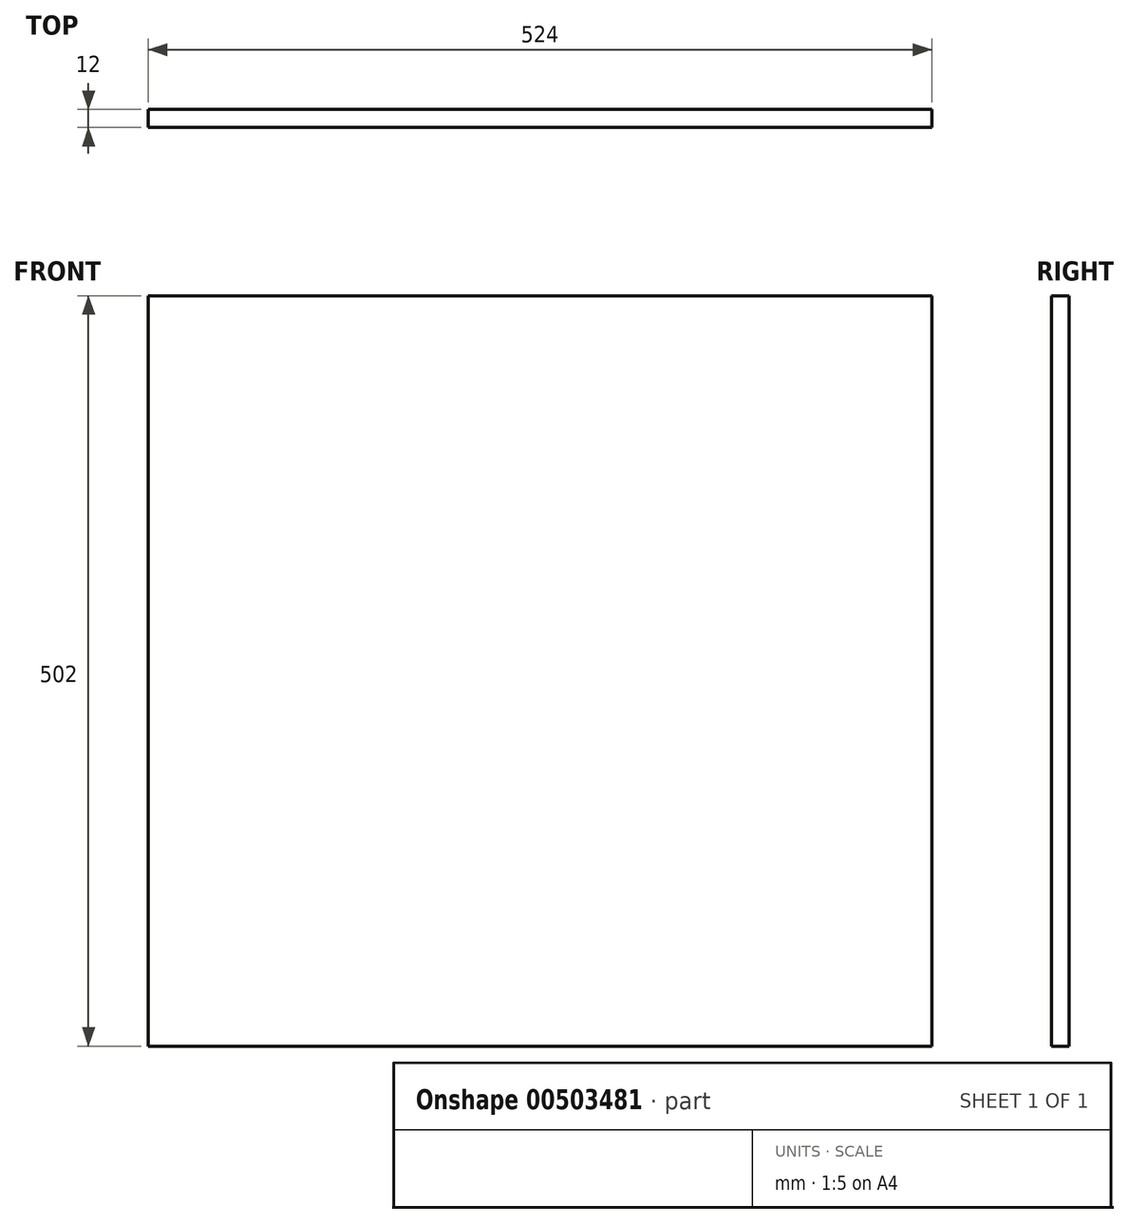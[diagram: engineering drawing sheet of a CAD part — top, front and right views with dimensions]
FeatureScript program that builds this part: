
annotation { "Feature Type Name" : "Feature", "Feature Type Description" : "" }
export const myFeature = defineFeature(function(context is Context, id is Id, definition is map)
    precondition{}
    {
        {
            var Q0;
            Q0=qCreatedBy(makeId("Top.planeOp"),FACE);
            var sketch = newSketch(context, id + "F0", { "sketchPlane" : qUnion([Q0])});
            skLineSegment(sketch, "E0.bottom", {"start": v(250, -250) * mm, "end": v(-250, -250) * mm});
            skLineSegment(sketch, "E0.top", {"start": v(250, 250) * mm, "end": v(-250, 250) * mm});
            skLineSegment(sketch, "E0.left", {"start": v(250, -250) * mm, "end": v(250, 250) * mm});
            skLineSegment(sketch, "E0.right", {"start": v(-250, -250) * mm, "end": v(-250, 250) * mm});
            skPoint(sketch, "E0.middle", {"position": v(0, 0) * mm});
            skSolve(sketch);
        }
        {
            var Q0;
            Q0=qSketchRegion(id+"F0",true);
            extrude(context, id + "F1", {"entities" : qUnion([Q0]), "depth" : 12 * mm, "offsetDistance" : 25 * mm});
        }
        {
            var Q0;
            Q0=qCreatedBy(makeId("Right.planeOp"),FACE);
            var sketch = newSketch(context, id + "F2", { "sketchPlane" : qUnion([Q0])});
            skLineSegment(sketch, "E1.bottom", {"start": v(250, -25) * mm, "end": v(-250, -25) * mm});
            skLineSegment(sketch, "E1.top", {"start": v(250, 25) * mm, "end": v(-250, 25) * mm});
            skLineSegment(sketch, "E1.left", {"start": v(250, -25) * mm, "end": v(250, 25) * mm});
            skLineSegment(sketch, "E1.right", {"start": v(-250, -25) * mm, "end": v(-250, 25) * mm});
            skPoint(sketch, "E1.middle", {"position": v(0, 0) * mm});
            skSolve(sketch);
        }
        {
            var Q0;
            Q0=qSketchRegion(id+"F2",true);
            extrude(context, id + "F3", {"entities" : qUnion([Q0]), "endBound" : BoundingType.SYMMETRIC, "depth" : 12 * mm, "offsetDistance" : 25 * mm});
        }
        {
            var Q0;
            Q0=makeQuery(id+"F3.opExtrude","SWEPT_BODY",BODY,{"disambiguationData":[OSD([sQuery(id+"F2.wireOp",EDGE,"E1.bottom"),sQuery(id+"F2.wireOp",EDGE,"E1.top"),sQuery(id+"F2.wireOp",EDGE,"E1.left"),sQuery(id+"F2.wireOp",EDGE,"E1.right")])]});
            transform(context, id + "F4", {"entities" : qUnion([Q0]), "transformType" : TransformType.TRANSLATION_3D, "dx" : 0 * mm, "dy" : 0 * mm, "dz" : -25 * mm, "makeCopy" : false});
        }
        {
            var Q0;
            Q0=qCreatedBy(makeId("Front.planeOp"),FACE);
            var sketch = newSketch(context, id + "F5", { "sketchPlane" : qUnion([Q0])});
            skLineSegment(sketch, "E2.bottom", {"start": v(250, -25) * mm, "end": v(-250, -25) * mm});
            skLineSegment(sketch, "E2.left", {"start": v(250, -25) * mm, "end": v(250, 25) * mm});
            skLineSegment(sketch, "E2.right", {"start": v(-250, -25) * mm, "end": v(-250, 25) * mm});
            skPoint(sketch, "E2.middle", {"position": v(0, 0) * mm});
            skLineSegment(sketch, "E3", {"start": v(-250, 25) * mm, "end": v(-6, 25) * mm});
            skLineSegment(sketch, "E4", {"start": v(-6, 25) * mm, "end": v(-6, 0) * mm});
            skLineSegment(sketch, "E5", {"start": v(-6, 0) * mm, "end": v(6, 0) * mm});
            skLineSegment(sketch, "E6", {"start": v(6, 0) * mm, "end": v(6, 25) * mm});
            skLineSegment(sketch, "E7", {"start": v(6, 25) * mm, "end": v(250, 25) * mm});
            skSolve(sketch);
        }
        {
            var Q0;
            Q0=qSketchRegion(id+"F5",true);
            extrude(context, id + "F6", {"entities" : qUnion([Q0]), "endBound" : BoundingType.SYMMETRIC, "depth" : 12 * mm, "offsetDistance" : 25 * mm});
        }
        {
            var Q0;
            Q0=makeQuery(id+"F6.opExtrude","SWEPT_BODY",BODY,{"disambiguationData":[OSD([sQuery(id+"F5.wireOp",EDGE,"E2.bottom"),sQuery(id+"F5.wireOp",EDGE,"E2.top"),sQuery(id+"F5.wireOp",EDGE,"E2.left"),sQuery(id+"F5.wireOp",EDGE,"E2.right")])]});
            transform(context, id + "F7", {"entities" : qUnion([Q0]), "transformType" : TransformType.TRANSLATION_3D, "dx" : 0 * mm, "dy" : 80 * mm, "dz" : -25 * mm, "makeCopy" : false});
        }
        {
            var Q0;
            Q0=makeQuery(id+"F6.opExtrude","SWEPT_BODY",BODY,{"disambiguationData":[OSD([sQuery(id+"F5.wireOp",EDGE,"E2.bottom"),sQuery(id+"F5.wireOp",EDGE,"E2.top"),sQuery(id+"F5.wireOp",EDGE,"E2.left"),sQuery(id+"F5.wireOp",EDGE,"E2.right")])]});
            transform(context, id + "F8", {"entities" : qUnion([Q0]), "transformType" : TransformType.COPY});
        }
        {
            var Q0;
            Q0=makeQuery(id+"F8.opPattern","COPY",BODY,{"derivedFrom":makeQuery(id+"F6.opExtrude","SWEPT_BODY",BODY,{"disambiguationData":[OSD([sQuery(id+"F5.wireOp",EDGE,"E2.bottom"),sQuery(id+"F5.wireOp",EDGE,"E2.top"),sQuery(id+"F5.wireOp",EDGE,"E2.left"),sQuery(id+"F5.wireOp",EDGE,"E2.right")])]}),"instanceName":"1"});
            deleteBodies(context, id + "F9", {"entities" : qUnion([Q0])});
        }
        {
            var Q0;
            Q0=makeQuery(id+"F6.opExtrude","SWEPT_BODY",BODY,{"disambiguationData":[OSD([sQuery(id+"F5.wireOp",EDGE,"E2.bottom"),sQuery(id+"F5.wireOp",EDGE,"E2.left"),sQuery(id+"F5.wireOp",EDGE,"E2.right"),sQuery(id+"F5.wireOp",EDGE,"E3"),sQuery(id+"F5.wireOp",EDGE,"E4"),sQuery(id+"F5.wireOp",EDGE,"E5"),sQuery(id+"F5.wireOp",EDGE,"E6"),sQuery(id+"F5.wireOp",EDGE,"E7")])]});
            var Q1;
            Q1=makeQuery(id+"F3.opExtrude","SWEPT_BODY",BODY,{"disambiguationData":[OSD([sQuery(id+"F2.wireOp",EDGE,"E1.bottom"),sQuery(id+"F2.wireOp",EDGE,"E1.top"),sQuery(id+"F2.wireOp",EDGE,"E1.left"),sQuery(id+"F2.wireOp",EDGE,"E1.right")])]});
            booleanBodies(context, id + "F10", {"operationType" : BooleanOperationType.SUBTRACTION, "tools" : qUnion([Q0]), "targets" : qUnion([Q1]), "keepTools" : true});
        }
        {
            var Q0;
            Q0=makeQuery(id+"F6.opExtrude","SWEPT_BODY",BODY,{"disambiguationData":[OSD([sQuery(id+"F5.wireOp",EDGE,"E2.bottom"),sQuery(id+"F5.wireOp",EDGE,"E2.left"),sQuery(id+"F5.wireOp",EDGE,"E2.right"),sQuery(id+"F5.wireOp",EDGE,"E3"),sQuery(id+"F5.wireOp",EDGE,"E4"),sQuery(id+"F5.wireOp",EDGE,"E5"),sQuery(id+"F5.wireOp",EDGE,"E6"),sQuery(id+"F5.wireOp",EDGE,"E7")])]});
            transform(context, id + "F11", {"entities" : qUnion([Q0]), "transformType" : TransformType.TRANSLATION_3D, "dx" : 0 * mm, "dy" : 164 * mm, "dz" : 0 * mm, "makeCopy" : true});
        }
        {
            var Q0;
            Q0=makeQuery(id+"F11.opPattern","COPY",BODY,{"derivedFrom":makeQuery(id+"F6.opExtrude","SWEPT_BODY",BODY,{"disambiguationData":[OSD([sQuery(id+"F5.wireOp",EDGE,"E2.bottom"),sQuery(id+"F5.wireOp",EDGE,"E2.left"),sQuery(id+"F5.wireOp",EDGE,"E2.right"),sQuery(id+"F5.wireOp",EDGE,"E3"),sQuery(id+"F5.wireOp",EDGE,"E4"),sQuery(id+"F5.wireOp",EDGE,"E5"),sQuery(id+"F5.wireOp",EDGE,"E6"),sQuery(id+"F5.wireOp",EDGE,"E7")])]}),"instanceName":"1"});
            var Q1;
            Q1=makeQuery(id+"F3.opExtrude","SWEPT_BODY",BODY,{"disambiguationData":[OSD([sQuery(id+"F2.wireOp",EDGE,"E1.bottom"),sQuery(id+"F2.wireOp",EDGE,"E1.top"),sQuery(id+"F2.wireOp",EDGE,"E1.left"),sQuery(id+"F2.wireOp",EDGE,"E1.right")])]});
            booleanBodies(context, id + "F12", {"operationType" : BooleanOperationType.SUBTRACTION, "tools" : qUnion([Q0]), "targets" : qUnion([Q1]), "keepTools" : true});
        }
        {
            var Q0;
            Q0=qCreatedBy(makeId("Right.planeOp"),FACE);
            var sketch = newSketch(context, id + "F13", { "sketchPlane" : qUnion([Q0])});
            skLineSegment(sketch, "E8", {"start": v(0, 0) * mm, "end": v(250, 0) * mm});
            skLineSegment(sketch, "E9", {"start": v(250, 0) * mm, "end": v(250, -50) * mm});
            skLineSegment(sketch, "E10", {"start": v(250, -50) * mm, "end": v(-250, -50) * mm});
            skLineSegment(sketch, "E11", {"start": v(-250, -50) * mm, "end": v(-250, 100) * mm});
            skLineSegment(sketch, "E12", {"start": v(250, 0) * mm, "end": v(250, 452) * mm});
            skLineSegment(sketch, "E13", {"start": v(250, 452) * mm, "end": v(-110, 452) * mm});
            skLineSegment(sketch, "E14", {"start": v(-110, 452) * mm, "end": v(-250, 100) * mm});
            skLineSegment(sketch, "E15", {"start": v(250, 452) * mm, "end": v(70, 452) * mm});
            skLineSegment(sketch, "E16", {"start": v(70, 452) * mm, "end": v(70, 392) * mm});
            skLineSegment(sketch, "E17.bottom", {"start": v(140, 372) * mm, "end": v(0, 372) * mm});
            skLineSegment(sketch, "E17.top", {"start": v(140, 412) * mm, "end": v(0, 412) * mm});
            skLineSegment(sketch, "E17.left", {"start": v(140, 372) * mm, "end": v(140, 412) * mm});
            skLineSegment(sketch, "E17.right", {"start": v(0, 372) * mm, "end": v(0, 412) * mm});
            skPoint(sketch, "E17.middle", {"position": v(70, 392) * mm});
            skSolve(sketch);
        }
        {
            var Q0;
            Q0=makeQuery(id+"F13.imprint","IMPRINT",FACE,{"disambiguationData":[TD([[makeQuery(id+"F13.imprint","IMPRINT",EDGE,{"derivedFrom":sQuery(id+"F13.wireOp",EDGE,"E9")}),-1.0]])]});
            extrude(context, id + "F14", {"entities" : qUnion([Q0]), "endBound" : BoundingType.SYMMETRIC, "depth" : 12 * mm, "offsetDistance" : 25 * mm});
        }
        {
            var Q0;
            Q0=makeQuery(id+"F14.opExtrude","SWEPT_EDGE",EDGE,{"disambiguationData":[OSD([sQuery(id+"F13.wireOp",EDGE,"E17.bottom"),sQuery(id+"F13.wireOp",EDGE,"E17.left")])]});
            var Q1;
            Q1=makeQuery(id+"F14.opExtrude","SWEPT_EDGE",EDGE,{"disambiguationData":[OSD([sQuery(id+"F13.wireOp",EDGE,"E17.top"),sQuery(id+"F13.wireOp",EDGE,"E17.left")])]});
            var Q2;
            Q2=makeQuery(id+"F14.opExtrude","SWEPT_EDGE",EDGE,{"disambiguationData":[OSD([sQuery(id+"F13.wireOp",EDGE,"E17.top"),sQuery(id+"F13.wireOp",EDGE,"E17.right")])]});
            var Q3;
            Q3=makeQuery(id+"F14.opExtrude","SWEPT_EDGE",EDGE,{"disambiguationData":[OSD([sQuery(id+"F13.wireOp",EDGE,"E17.bottom"),sQuery(id+"F13.wireOp",EDGE,"E17.right")])]});
            fillet(context, id + "F15", {"entities" : qUnion([Q0, Q1, Q2, Q3]), "radius" : 20 * mm, "tangentPropagation" : true, "allowEdgeOverflow" : false});
        }
        {
            var Q0;
            Q0=makeQuery(id+"F14.opExtrude","SWEPT_BODY",BODY,{"disambiguationData":[OSD([sQuery(id+"F13.wireOp",EDGE,"E9"),sQuery(id+"F13.wireOp",EDGE,"E10"),sQuery(id+"F13.wireOp",EDGE,"E11"),sQuery(id+"F13.wireOp",EDGE,"E12"),sQuery(id+"F13.wireOp",EDGE,"E13"),sQuery(id+"F13.wireOp",EDGE,"E14"),sQuery(id+"F13.wireOp",EDGE,"E17.bottom"),sQuery(id+"F13.wireOp",EDGE,"E17.top"),sQuery(id+"F13.wireOp",EDGE,"E17.left"),sQuery(id+"F13.wireOp",EDGE,"E17.right")])]});
            transform(context, id + "F16", {"entities" : qUnion([Q0]), "transformType" : TransformType.TRANSLATION_3D, "dx" : -256 * mm, "dy" : 0 * mm, "dz" : 0 * mm, "makeCopy" : false});
        }
        {
            var Q0;
            Q0=makeQuery(id+"F14.opExtrude","SWEPT_BODY",BODY,{"disambiguationData":[OSD([sQuery(id+"F13.wireOp",EDGE,"E9"),sQuery(id+"F13.wireOp",EDGE,"E10"),sQuery(id+"F13.wireOp",EDGE,"E11"),sQuery(id+"F13.wireOp",EDGE,"E12"),sQuery(id+"F13.wireOp",EDGE,"E13"),sQuery(id+"F13.wireOp",EDGE,"E14"),sQuery(id+"F13.wireOp",EDGE,"E17.bottom"),sQuery(id+"F13.wireOp",EDGE,"E17.top"),sQuery(id+"F13.wireOp",EDGE,"E17.left"),sQuery(id+"F13.wireOp",EDGE,"E17.right")])]});
            transform(context, id + "F17", {"entities" : qUnion([Q0]), "transformType" : TransformType.TRANSLATION_3D, "dx" : 512 * mm, "dy" : 0 * mm, "dz" : 0 * mm, "makeCopy" : true});
        }
        {
            var Q0;
            Q0=qCreatedBy(makeId("Front.planeOp"),FACE);
            var sketch = newSketch(context, id + "F18", { "sketchPlane" : qUnion([Q0])});
            skLineSegment(sketch, "E18", {"start": v(0, 0) * mm, "end": v(-262, 0) * mm});
            skLineSegment(sketch, "E19", {"start": v(-262, 0) * mm, "end": v(-262, -50) * mm});
            skLineSegment(sketch, "E20", {"start": v(-262, -50) * mm, "end": v(262, -50) * mm});
            skLineSegment(sketch, "E21", {"start": v(262, -50) * mm, "end": v(262, 452) * mm});
            skLineSegment(sketch, "E22", {"start": v(262, 452) * mm, "end": v(-262, 452) * mm});
            skLineSegment(sketch, "E23", {"start": v(-262, 452) * mm, "end": v(-262, 0) * mm});
            skSolve(sketch);
        }
        {
            var Q0;
            Q0=qSketchRegion(id+"F18",true);
            extrude(context, id + "F19", {"entities" : qUnion([Q0]), "endBound" : BoundingType.SYMMETRIC, "depth" : 12 * mm, "offsetDistance" : 25 * mm});
        }
        {
            var Q0;
            Q0=makeQuery(id+"F19.opExtrude","SWEPT_BODY",BODY,{"disambiguationData":[OSD([sQuery(id+"F18.wireOp",EDGE,"E19"),sQuery(id+"F18.wireOp",EDGE,"E20"),sQuery(id+"F18.wireOp",EDGE,"E21"),sQuery(id+"F18.wireOp",EDGE,"E22"),sQuery(id+"F18.wireOp",EDGE,"E23")])]});
            transform(context, id + "F20", {"entities" : qUnion([Q0]), "transformType" : TransformType.TRANSLATION_3D, "dx" : 0 * mm, "dy" : 256 * mm, "dz" : 0 * mm, "makeCopy" : false});
        }
        {
            var Q0;
            Q0=makeQuery(id+"F1.opExtrude","CAP_FACE",FACE,{"disambiguationData":[OSD([sQuery(id+"F0.wireOp",EDGE,"E0.bottom"),sQuery(id+"F0.wireOp",EDGE,"E0.top"),sQuery(id+"F0.wireOp",EDGE,"E0.left"),sQuery(id+"F0.wireOp",EDGE,"E0.right")])],"isStart":false});
            var sketch = newSketch(context, id + "F21", { "sketchPlane" : qUnion([Q0])});
            skLineSegment(sketch, "E24", {"start": v(0, 0) * mm, "end": v(0, 262) * mm});
            skLineSegment(sketch, "E25", {"start": v(0, 262) * mm, "end": v(262, 262) * mm});
            skLineSegment(sketch, "E26", {"start": v(262, 262) * mm, "end": v(262, -110) * mm});
            skLineSegment(sketch, "E27", {"start": v(262, -110) * mm, "end": v(-262, -110) * mm});
            skLineSegment(sketch, "E28", {"start": v(-262, -110) * mm, "end": v(-262, 262) * mm});
            skLineSegment(sketch, "E29", {"start": v(-262, 262) * mm, "end": v(0, 262) * mm});
            skSolve(sketch);
        }
        {
            var Q0;
            Q0=qSketchRegion(id+"F21",true);
            extrude(context, id + "F22", {"entities" : qUnion([Q0]), "depth" : 12 * mm, "offsetDistance" : 25 * mm});
        }
        {
            var Q0;
            Q0=makeQuery(id+"F22.opExtrude","SWEPT_BODY",BODY,{"disambiguationData":[OSD([sQuery(id+"F21.wireOp",EDGE,"E25"),sQuery(id+"F21.wireOp",EDGE,"E26"),sQuery(id+"F21.wireOp",EDGE,"E27"),sQuery(id+"F21.wireOp",EDGE,"E28"),sQuery(id+"F21.wireOp",EDGE,"E29")])]});
            transform(context, id + "F23", {"entities" : qUnion([Q0]), "transformType" : TransformType.TRANSLATION_3D, "dx" : 0 * mm, "dy" : 0 * mm, "dz" : 440 * mm, "makeCopy" : false});
        }
        {
            var Q0;
            Q0=qCreatedBy(makeId("Front.planeOp"),FACE);
            var sketch = newSketch(context, id + "F24", { "sketchPlane" : qUnion([Q0])});
            skLineSegment(sketch, "E30", {"start": v(0, 0) * mm, "end": v(0, 12) * mm});
            skLineSegment(sketch, "E31", {"start": v(0, 12) * mm, "end": v(250, 12) * mm});
            skLineSegment(sketch, "E32", {"start": v(250, 12) * mm, "end": v(250, 100) * mm});
            skLineSegment(sketch, "E33", {"start": v(250, 100) * mm, "end": v(-250, 100) * mm});
            skLineSegment(sketch, "E34", {"start": v(-250, 100) * mm, "end": v(-250, 12) * mm});
            skLineSegment(sketch, "E35", {"start": v(-250, 12) * mm, "end": v(0, 12) * mm});
            skSolve(sketch);
        }
        {
            var Q0;
            Q0=qSketchRegion(id+"F24",true);
            extrude(context, id + "F25", {"entities" : qUnion([Q0]), "endBound" : BoundingType.SYMMETRIC, "depth" : 12 * mm, "offsetDistance" : 25 * mm});
        }
        {
            var Q0;
            Q0=makeQuery(id+"F25.opExtrude","SWEPT_BODY",BODY,{"disambiguationData":[OSD([sQuery(id+"F24.wireOp",EDGE,"E31"),sQuery(id+"F24.wireOp",EDGE,"E32"),sQuery(id+"F24.wireOp",EDGE,"E33"),sQuery(id+"F24.wireOp",EDGE,"E34"),sQuery(id+"F24.wireOp",EDGE,"E35")])]});
            transform(context, id + "F26", {"entities" : qUnion([Q0]), "transformType" : TransformType.TRANSLATION_3D, "dx" : 0 * mm, "dy" : -244 * mm, "dz" : 0 * mm, "makeCopy" : false});
        }
        {
            var Q0;
            Q0=qCreatedBy(makeId("Top.planeOp"),FACE);
            var sketch = newSketch(context, id + "F27", { "sketchPlane" : qUnion([Q0])});
            skLineSegment(sketch, "E36", {"start": v(0, 0) * mm, "end": v(0, 70) * mm});
            skLineSegment(sketch, "E37", {"start": v(0, 70) * mm, "end": v(-18, 70) * mm});
            skLineSegment(sketch, "E38", {"start": v(-18, 70) * mm, "end": v(-18, -250) * mm});
            skLineSegment(sketch, "E39", {"start": v(-18, -250) * mm, "end": v(-30, -250) * mm});
            skLineSegment(sketch, "E40", {"start": v(-30, -250) * mm, "end": v(-30, 70) * mm});
            skLineSegment(sketch, "E41", {"start": v(-30, 70) * mm, "end": v(-18, 70) * mm});
            skSolve(sketch);
        }
        {
            var Q0;
            Q0=qSketchRegion(id+"F27",true);
            extrude(context, id + "F28", {"entities" : qUnion([Q0]), "depth" : 44 * mm, "offsetDistance" : 25 * mm});
        }
        {
            var Q0;
            Q0=makeQuery(id+"F28.opExtrude","SWEPT_BODY",BODY,{"disambiguationData":[OSD([sQuery(id+"F27.wireOp",EDGE,"E38"),sQuery(id+"F27.wireOp",EDGE,"E39"),sQuery(id+"F27.wireOp",EDGE,"E40"),sQuery(id+"F27.wireOp",EDGE,"E41")])]});
            transform(context, id + "F29", {"entities" : qUnion([Q0]), "transformType" : TransformType.TRANSLATION_3D, "dx" : 0 * mm, "dy" : 0 * mm, "dz" : -48 * mm, "makeCopy" : false});
        }
        {
            var Q0;
            Q0=makeQuery(id+"F28.opExtrude","SWEPT_BODY",BODY,{"disambiguationData":[OSD([sQuery(id+"F27.wireOp",EDGE,"E38"),sQuery(id+"F27.wireOp",EDGE,"E39"),sQuery(id+"F27.wireOp",EDGE,"E40"),sQuery(id+"F27.wireOp",EDGE,"E41")])]});
            transform(context, id + "F30", {"entities" : qUnion([Q0]), "transformType" : TransformType.TRANSLATION_3D, "dx" : -208 * mm, "dy" : 0 * mm, "dz" : 0 * mm, "makeCopy" : true});
        }
        {
            var Q0;
            Q0=qCreatedBy(makeId("Top.planeOp"),FACE);
            var sketch = newSketch(context, id + "F31", { "sketchPlane" : qUnion([Q0])});
            skLineSegment(sketch, "E42", {"start": v(0, 0) * mm, "end": v(0, -250) * mm});
            skLineSegment(sketch, "E43", {"start": v(0, -250) * mm, "end": v(-30, -250) * mm});
            skLineSegment(sketch, "E44", {"start": v(-30, -250) * mm, "end": v(-226, -250) * mm});
            skLineSegment(sketch, "E45", {"start": v(-226, -250) * mm, "end": v(-226, -238) * mm});
            skLineSegment(sketch, "E46", {"start": v(-226, -238) * mm, "end": v(-30, -238) * mm});
            skLineSegment(sketch, "E47", {"start": v(-30, -238) * mm, "end": v(-30, -250) * mm});
            skSolve(sketch);
        }
        {
            var Q0;
            Q0=qSketchRegion(id+"F31",true);
            extrude(context, id + "F32", {"entities" : qUnion([Q0]), "depth" : -44 * mm, "offsetDistance" : 25 * mm});
        }
        {
            var Q0;
            Q0=makeQuery(id+"F32.opExtrude","SWEPT_BODY",BODY,{"disambiguationData":[OSD([sQuery(id+"F31.wireOp",EDGE,"E44"),sQuery(id+"F31.wireOp",EDGE,"E45"),sQuery(id+"F31.wireOp",EDGE,"E46"),sQuery(id+"F31.wireOp",EDGE,"E47")])]});
            transform(context, id + "F33", {"entities" : qUnion([Q0]), "transformType" : TransformType.TRANSLATION_3D, "dx" : 0 * mm, "dy" : 0 * mm, "dz" : -4 * mm, "makeCopy" : false});
        }
        {
            var Q0;
            Q0=makeQuery(id+"F32.opExtrude","SWEPT_BODY",BODY,{"disambiguationData":[OSD([sQuery(id+"F31.wireOp",EDGE,"E44"),sQuery(id+"F31.wireOp",EDGE,"E45"),sQuery(id+"F31.wireOp",EDGE,"E46"),sQuery(id+"F31.wireOp",EDGE,"E47")])]});
            transform(context, id + "F34", {"entities" : qUnion([Q0]), "transformType" : TransformType.TRANSLATION_3D, "dx" : 0 * mm, "dy" : 308 * mm, "dz" : 0 * mm, "makeCopy" : true});
        }
        {
            var Q0;
            Q0=makeQuery(id+"F32.opExtrude","SWEPT_BODY",BODY,{"disambiguationData":[OSD([sQuery(id+"F31.wireOp",EDGE,"E44"),sQuery(id+"F31.wireOp",EDGE,"E45"),sQuery(id+"F31.wireOp",EDGE,"E46"),sQuery(id+"F31.wireOp",EDGE,"E47")])]});
            var Q1;
            Q1=makeQuery(id+"F30.opPattern","COPY",BODY,{"derivedFrom":makeQuery(id+"F28.opExtrude","SWEPT_BODY",BODY,{"disambiguationData":[OSD([sQuery(id+"F27.wireOp",EDGE,"E38"),sQuery(id+"F27.wireOp",EDGE,"E39"),sQuery(id+"F27.wireOp",EDGE,"E40"),sQuery(id+"F27.wireOp",EDGE,"E41")])]}),"instanceName":"1"});
            var Q2;
            Q2=makeQuery(id+"F28.opExtrude","SWEPT_BODY",BODY,{"disambiguationData":[OSD([sQuery(id+"F27.wireOp",EDGE,"E38"),sQuery(id+"F27.wireOp",EDGE,"E39"),sQuery(id+"F27.wireOp",EDGE,"E40"),sQuery(id+"F27.wireOp",EDGE,"E41")])]});
            var Q3;
            Q3=makeQuery(id+"F34.opPattern","COPY",BODY,{"derivedFrom":makeQuery(id+"F32.opExtrude","SWEPT_BODY",BODY,{"disambiguationData":[OSD([sQuery(id+"F31.wireOp",EDGE,"E44"),sQuery(id+"F31.wireOp",EDGE,"E45"),sQuery(id+"F31.wireOp",EDGE,"E46"),sQuery(id+"F31.wireOp",EDGE,"E47")])]}),"instanceName":"1"});
            transform(context, id + "F35", {"entities" : qUnion([Q0, Q1, Q2, Q3]), "transformType" : TransformType.TRANSLATION_3D, "dx" : 256 * mm, "dy" : 0 * mm, "dz" : 0 * mm, "makeCopy" : true});
        }
        {
            var Q0;
            Q0=qCreatedBy(makeId("Top.planeOp"),FACE);
            var sketch = newSketch(context, id + "F36", { "sketchPlane" : qUnion([Q0])});
            skLineSegment(sketch, "E48", {"start": v(0, 0) * mm, "end": v(-24, 0) * mm});
            skLineSegment(sketch, "E49", {"start": v(-24, 0) * mm, "end": v(-24, -244) * mm});
            skLineSegment(sketch, "E50", {"start": v(-24, -244) * mm, "end": v(-232, -244) * mm});
            skLineSegment(sketch, "E51", {"start": v(-232, -244) * mm, "end": v(-232, 64) * mm});
            skLineSegment(sketch, "E52", {"start": v(-232, 64) * mm, "end": v(-24, 64) * mm});
            skLineSegment(sketch, "E53", {"start": v(-24, 64) * mm, "end": v(-24, 0) * mm});
            skSolve(sketch);
        }
        {
            var Q0;
            Q0=qSketchRegion(id+"F36",true);
            extrude(context, id + "F37", {"entities" : qUnion([Q0]), "depth" : 3 * mm, "offsetDistance" : 25 * mm});
        }
        {
            var Q0;
            Q0=makeQuery(id+"F37.opExtrude","SWEPT_BODY",BODY,{"disambiguationData":[OSD([sQuery(id+"F36.wireOp",EDGE,"E49"),sQuery(id+"F36.wireOp",EDGE,"E50"),sQuery(id+"F36.wireOp",EDGE,"E51"),sQuery(id+"F36.wireOp",EDGE,"E52"),sQuery(id+"F36.wireOp",EDGE,"E53")])]});
            transform(context, id + "F38", {"entities" : qUnion([Q0]), "transformType" : TransformType.TRANSLATION_3D, "dx" : 0 * mm, "dy" : 0 * mm, "dz" : -44 * mm, "makeCopy" : false});
        }
        {
            var Q0;
            Q0=makeQuery(id+"F37.opExtrude","SWEPT_BODY",BODY,{"disambiguationData":[OSD([sQuery(id+"F36.wireOp",EDGE,"E49"),sQuery(id+"F36.wireOp",EDGE,"E50"),sQuery(id+"F36.wireOp",EDGE,"E51"),sQuery(id+"F36.wireOp",EDGE,"E52"),sQuery(id+"F36.wireOp",EDGE,"E53")])]});
            transform(context, id + "F39", {"entities" : qUnion([Q0]), "transformType" : TransformType.TRANSLATION_3D, "dx" : 256 * mm, "dy" : 0 * mm, "dz" : 0 * mm, "makeCopy" : true});
        }
        {
            var Q0;
            Q0=makeQuery(id+"F37.opExtrude","SWEPT_BODY",BODY,{"disambiguationData":[OSD([sQuery(id+"F36.wireOp",EDGE,"E49"),sQuery(id+"F36.wireOp",EDGE,"E50"),sQuery(id+"F36.wireOp",EDGE,"E51"),sQuery(id+"F36.wireOp",EDGE,"E52"),sQuery(id+"F36.wireOp",EDGE,"E53")])]});
            var Q1;
            Q1=makeQuery(id+"F30.opPattern","COPY",BODY,{"derivedFrom":makeQuery(id+"F28.opExtrude","SWEPT_BODY",BODY,{"disambiguationData":[OSD([sQuery(id+"F27.wireOp",EDGE,"E38"),sQuery(id+"F27.wireOp",EDGE,"E39"),sQuery(id+"F27.wireOp",EDGE,"E40"),sQuery(id+"F27.wireOp",EDGE,"E41")])]}),"instanceName":"1"});
            var Q2;
            Q2=makeQuery(id+"F32.opExtrude","SWEPT_BODY",BODY,{"disambiguationData":[OSD([sQuery(id+"F31.wireOp",EDGE,"E44"),sQuery(id+"F31.wireOp",EDGE,"E45"),sQuery(id+"F31.wireOp",EDGE,"E46"),sQuery(id+"F31.wireOp",EDGE,"E47")])]});
            var Q3;
            Q3=makeQuery(id+"F28.opExtrude","SWEPT_BODY",BODY,{"disambiguationData":[OSD([sQuery(id+"F27.wireOp",EDGE,"E38"),sQuery(id+"F27.wireOp",EDGE,"E39"),sQuery(id+"F27.wireOp",EDGE,"E40"),sQuery(id+"F27.wireOp",EDGE,"E41")])]});
            var Q4;
            Q4=makeQuery(id+"F34.opPattern","COPY",BODY,{"derivedFrom":makeQuery(id+"F32.opExtrude","SWEPT_BODY",BODY,{"disambiguationData":[OSD([sQuery(id+"F31.wireOp",EDGE,"E44"),sQuery(id+"F31.wireOp",EDGE,"E45"),sQuery(id+"F31.wireOp",EDGE,"E46"),sQuery(id+"F31.wireOp",EDGE,"E47")])]}),"instanceName":"1"});
            booleanBodies(context, id + "F40", {"operationType" : BooleanOperationType.SUBTRACTION, "tools" : qUnion([Q0]), "targets" : qUnion([Q1, Q2, Q3, Q4]), "keepTools" : true});
        }
        {
            var Q0;
            Q0=makeQuery(id+"F39.opPattern","COPY",BODY,{"derivedFrom":makeQuery(id+"F37.opExtrude","SWEPT_BODY",BODY,{"disambiguationData":[OSD([sQuery(id+"F36.wireOp",EDGE,"E49"),sQuery(id+"F36.wireOp",EDGE,"E50"),sQuery(id+"F36.wireOp",EDGE,"E51"),sQuery(id+"F36.wireOp",EDGE,"E52"),sQuery(id+"F36.wireOp",EDGE,"E53")])]}),"instanceName":"1"});
            var Q1;
            Q1=makeQuery(id+"F35.opPattern","COPY",BODY,{"derivedFrom":makeQuery(id+"F32.opExtrude","SWEPT_BODY",BODY,{"disambiguationData":[OSD([sQuery(id+"F31.wireOp",EDGE,"E44"),sQuery(id+"F31.wireOp",EDGE,"E45"),sQuery(id+"F31.wireOp",EDGE,"E46"),sQuery(id+"F31.wireOp",EDGE,"E47")])]}),"instanceName":"1"});
            var Q2;
            Q2=makeQuery(id+"F35.opPattern","COPY",BODY,{"derivedFrom":makeQuery(id+"F28.opExtrude","SWEPT_BODY",BODY,{"disambiguationData":[OSD([sQuery(id+"F27.wireOp",EDGE,"E38"),sQuery(id+"F27.wireOp",EDGE,"E39"),sQuery(id+"F27.wireOp",EDGE,"E40"),sQuery(id+"F27.wireOp",EDGE,"E41")])]}),"instanceName":"1"});
            var Q3;
            Q3=makeQuery(id+"F35.opPattern","COPY",BODY,{"derivedFrom":makeQuery(id+"F34.opPattern","COPY",BODY,{"derivedFrom":makeQuery(id+"F32.opExtrude","SWEPT_BODY",BODY,{"disambiguationData":[OSD([sQuery(id+"F31.wireOp",EDGE,"E44"),sQuery(id+"F31.wireOp",EDGE,"E45"),sQuery(id+"F31.wireOp",EDGE,"E46"),sQuery(id+"F31.wireOp",EDGE,"E47")])]}),"instanceName":"1"}),"instanceName":"1"});
            var Q4;
            Q4=makeQuery(id+"F35.opPattern","COPY",BODY,{"derivedFrom":makeQuery(id+"F30.opPattern","COPY",BODY,{"derivedFrom":makeQuery(id+"F28.opExtrude","SWEPT_BODY",BODY,{"disambiguationData":[OSD([sQuery(id+"F27.wireOp",EDGE,"E38"),sQuery(id+"F27.wireOp",EDGE,"E39"),sQuery(id+"F27.wireOp",EDGE,"E40"),sQuery(id+"F27.wireOp",EDGE,"E41")])]}),"instanceName":"1"}),"instanceName":"1"});
            booleanBodies(context, id + "F41", {"operationType" : BooleanOperationType.SUBTRACTION, "tools" : qUnion([Q0]), "targets" : qUnion([Q1, Q2, Q3, Q4]), "keepTools" : true});
        }
        {
            var Q0;
            Q0=qCreatedBy(makeId("Front.planeOp"),FACE);
            var sketch = newSketch(context, id + "F42", { "sketchPlane" : qUnion([Q0])});
            skLineSegment(sketch, "E54", {"start": v(0, 0) * mm, "end": v(0, 12) * mm});
            skLineSegment(sketch, "E55", {"start": v(0, 12) * mm, "end": v(262, 12) * mm});
            skLineSegment(sketch, "E56", {"start": v(262, 12) * mm, "end": v(262, -50) * mm});
            skLineSegment(sketch, "E57", {"start": v(262, -50) * mm, "end": v(0, -50) * mm});
            skLineSegment(sketch, "E58", {"start": v(0, -50) * mm, "end": v(0, 0) * mm});
            skSolve(sketch);
        }
        {
            var Q0;
            Q0=qSketchRegion(id+"F42",true);
            extrude(context, id + "F43", {"entities" : qUnion([Q0]), "depth" : 12 * mm, "offsetDistance" : 25 * mm});
        }
        {
            var Q0;
            Q0=makeQuery(id+"F43.opExtrude","SWEPT_BODY",BODY,{"disambiguationData":[OSD([sQuery(id+"F42.wireOp",EDGE,"E54"),sQuery(id+"F42.wireOp",EDGE,"E55"),sQuery(id+"F42.wireOp",EDGE,"E56"),sQuery(id+"F42.wireOp",EDGE,"E57"),sQuery(id+"F42.wireOp",EDGE,"E58")])]});
            transform(context, id + "F44", {"entities" : qUnion([Q0]), "transformType" : TransformType.TRANSLATION_3D, "dx" : 0 * mm, "dy" : -250 * mm, "dz" : 0 * mm, "makeCopy" : false});
        }
        {
            var Q0;
            Q0=makeQuery(id+"F43.opExtrude","SWEPT_BODY",BODY,{"disambiguationData":[OSD([sQuery(id+"F42.wireOp",EDGE,"E54"),sQuery(id+"F42.wireOp",EDGE,"E55"),sQuery(id+"F42.wireOp",EDGE,"E56"),sQuery(id+"F42.wireOp",EDGE,"E57"),sQuery(id+"F42.wireOp",EDGE,"E58")])]});
            transform(context, id + "F45", {"entities" : qUnion([Q0]), "transformType" : TransformType.TRANSLATION_3D, "dx" : -262 * mm, "dy" : 0 * mm, "dz" : 0 * mm, "makeCopy" : true});
        }
        {
            var Q0;
            Q0=makeQuery(id+"F1.opExtrude","SWEPT_BODY",BODY,{"disambiguationData":[OSD([sQuery(id+"F0.wireOp",EDGE,"E0.bottom"),sQuery(id+"F0.wireOp",EDGE,"E0.top"),sQuery(id+"F0.wireOp",EDGE,"E0.left"),sQuery(id+"F0.wireOp",EDGE,"E0.right")])]});
            var Q1;
            Q1=makeQuery(id+"F3.opExtrude","SWEPT_BODY",BODY,{"disambiguationData":[OSD([sQuery(id+"F2.wireOp",EDGE,"E1.bottom"),sQuery(id+"F2.wireOp",EDGE,"E1.top"),sQuery(id+"F2.wireOp",EDGE,"E1.left"),sQuery(id+"F2.wireOp",EDGE,"E1.right")])]});
            var Q2;
            Q2=makeQuery(id+"F6.opExtrude","SWEPT_BODY",BODY,{"disambiguationData":[OSD([sQuery(id+"F5.wireOp",EDGE,"E2.bottom"),sQuery(id+"F5.wireOp",EDGE,"E2.left"),sQuery(id+"F5.wireOp",EDGE,"E2.right"),sQuery(id+"F5.wireOp",EDGE,"E3"),sQuery(id+"F5.wireOp",EDGE,"E4"),sQuery(id+"F5.wireOp",EDGE,"E5"),sQuery(id+"F5.wireOp",EDGE,"E6"),sQuery(id+"F5.wireOp",EDGE,"E7")])]});
            var Q3;
            Q3=makeQuery(id+"F11.opPattern","COPY",BODY,{"derivedFrom":makeQuery(id+"F6.opExtrude","SWEPT_BODY",BODY,{"disambiguationData":[OSD([sQuery(id+"F5.wireOp",EDGE,"E2.bottom"),sQuery(id+"F5.wireOp",EDGE,"E2.left"),sQuery(id+"F5.wireOp",EDGE,"E2.right"),sQuery(id+"F5.wireOp",EDGE,"E3"),sQuery(id+"F5.wireOp",EDGE,"E4"),sQuery(id+"F5.wireOp",EDGE,"E5"),sQuery(id+"F5.wireOp",EDGE,"E6"),sQuery(id+"F5.wireOp",EDGE,"E7")])]}),"instanceName":"1"});
            var Q4;
            Q4=makeQuery(id+"F14.opExtrude","SWEPT_BODY",BODY,{"disambiguationData":[OSD([sQuery(id+"F13.wireOp",EDGE,"E9"),sQuery(id+"F13.wireOp",EDGE,"E10"),sQuery(id+"F13.wireOp",EDGE,"E11"),sQuery(id+"F13.wireOp",EDGE,"E12"),sQuery(id+"F13.wireOp",EDGE,"E13"),sQuery(id+"F13.wireOp",EDGE,"E14"),sQuery(id+"F13.wireOp",EDGE,"E17.bottom"),sQuery(id+"F13.wireOp",EDGE,"E17.top"),sQuery(id+"F13.wireOp",EDGE,"E17.left"),sQuery(id+"F13.wireOp",EDGE,"E17.right")])]});
            var Q5;
            Q5=makeQuery(id+"F17.opPattern","COPY",BODY,{"derivedFrom":makeQuery(id+"F14.opExtrude","SWEPT_BODY",BODY,{"disambiguationData":[OSD([sQuery(id+"F13.wireOp",EDGE,"E9"),sQuery(id+"F13.wireOp",EDGE,"E10"),sQuery(id+"F13.wireOp",EDGE,"E11"),sQuery(id+"F13.wireOp",EDGE,"E12"),sQuery(id+"F13.wireOp",EDGE,"E13"),sQuery(id+"F13.wireOp",EDGE,"E14"),sQuery(id+"F13.wireOp",EDGE,"E17.bottom"),sQuery(id+"F13.wireOp",EDGE,"E17.top"),sQuery(id+"F13.wireOp",EDGE,"E17.left"),sQuery(id+"F13.wireOp",EDGE,"E17.right")])]}),"instanceName":"1"});
            var Q6;
            Q6=makeQuery(id+"F22.opExtrude","SWEPT_BODY",BODY,{"disambiguationData":[OSD([sQuery(id+"F21.wireOp",EDGE,"E25"),sQuery(id+"F21.wireOp",EDGE,"E26"),sQuery(id+"F21.wireOp",EDGE,"E27"),sQuery(id+"F21.wireOp",EDGE,"E28"),sQuery(id+"F21.wireOp",EDGE,"E29")])]});
            var Q7;
            Q7=makeQuery(id+"F25.opExtrude","SWEPT_BODY",BODY,{"disambiguationData":[OSD([sQuery(id+"F24.wireOp",EDGE,"E31"),sQuery(id+"F24.wireOp",EDGE,"E32"),sQuery(id+"F24.wireOp",EDGE,"E33"),sQuery(id+"F24.wireOp",EDGE,"E34"),sQuery(id+"F24.wireOp",EDGE,"E35")])]});
            var Q8;
            Q8=makeQuery(id+"F28.opExtrude","SWEPT_BODY",BODY,{"disambiguationData":[OSD([sQuery(id+"F27.wireOp",EDGE,"E38"),sQuery(id+"F27.wireOp",EDGE,"E39"),sQuery(id+"F27.wireOp",EDGE,"E40"),sQuery(id+"F27.wireOp",EDGE,"E41")])]});
            var Q9;
            Q9=makeQuery(id+"F30.opPattern","COPY",BODY,{"derivedFrom":makeQuery(id+"F28.opExtrude","SWEPT_BODY",BODY,{"disambiguationData":[OSD([sQuery(id+"F27.wireOp",EDGE,"E38"),sQuery(id+"F27.wireOp",EDGE,"E39"),sQuery(id+"F27.wireOp",EDGE,"E40"),sQuery(id+"F27.wireOp",EDGE,"E41")])]}),"instanceName":"1"});
            var Q10;
            Q10=makeQuery(id+"F32.opExtrude","SWEPT_BODY",BODY,{"disambiguationData":[OSD([sQuery(id+"F31.wireOp",EDGE,"E44"),sQuery(id+"F31.wireOp",EDGE,"E45"),sQuery(id+"F31.wireOp",EDGE,"E46"),sQuery(id+"F31.wireOp",EDGE,"E47")])]});
            var Q11;
            Q11=makeQuery(id+"F34.opPattern","COPY",BODY,{"derivedFrom":makeQuery(id+"F32.opExtrude","SWEPT_BODY",BODY,{"disambiguationData":[OSD([sQuery(id+"F31.wireOp",EDGE,"E44"),sQuery(id+"F31.wireOp",EDGE,"E45"),sQuery(id+"F31.wireOp",EDGE,"E46"),sQuery(id+"F31.wireOp",EDGE,"E47")])]}),"instanceName":"1"});
            var Q12;
            Q12=makeQuery(id+"F35.opPattern","COPY",BODY,{"derivedFrom":makeQuery(id+"F28.opExtrude","SWEPT_BODY",BODY,{"disambiguationData":[OSD([sQuery(id+"F27.wireOp",EDGE,"E38"),sQuery(id+"F27.wireOp",EDGE,"E39"),sQuery(id+"F27.wireOp",EDGE,"E40"),sQuery(id+"F27.wireOp",EDGE,"E41")])]}),"instanceName":"1"});
            var Q13;
            Q13=makeQuery(id+"F35.opPattern","COPY",BODY,{"derivedFrom":makeQuery(id+"F30.opPattern","COPY",BODY,{"derivedFrom":makeQuery(id+"F28.opExtrude","SWEPT_BODY",BODY,{"disambiguationData":[OSD([sQuery(id+"F27.wireOp",EDGE,"E38"),sQuery(id+"F27.wireOp",EDGE,"E39"),sQuery(id+"F27.wireOp",EDGE,"E40"),sQuery(id+"F27.wireOp",EDGE,"E41")])]}),"instanceName":"1"}),"instanceName":"1"});
            var Q14;
            Q14=makeQuery(id+"F35.opPattern","COPY",BODY,{"derivedFrom":makeQuery(id+"F32.opExtrude","SWEPT_BODY",BODY,{"disambiguationData":[OSD([sQuery(id+"F31.wireOp",EDGE,"E44"),sQuery(id+"F31.wireOp",EDGE,"E45"),sQuery(id+"F31.wireOp",EDGE,"E46"),sQuery(id+"F31.wireOp",EDGE,"E47")])]}),"instanceName":"1"});
            var Q15;
            Q15=makeQuery(id+"F35.opPattern","COPY",BODY,{"derivedFrom":makeQuery(id+"F34.opPattern","COPY",BODY,{"derivedFrom":makeQuery(id+"F32.opExtrude","SWEPT_BODY",BODY,{"disambiguationData":[OSD([sQuery(id+"F31.wireOp",EDGE,"E44"),sQuery(id+"F31.wireOp",EDGE,"E45"),sQuery(id+"F31.wireOp",EDGE,"E46"),sQuery(id+"F31.wireOp",EDGE,"E47")])]}),"instanceName":"1"}),"instanceName":"1"});
            var Q16;
            Q16=makeQuery(id+"F37.opExtrude","SWEPT_BODY",BODY,{"disambiguationData":[OSD([sQuery(id+"F36.wireOp",EDGE,"E49"),sQuery(id+"F36.wireOp",EDGE,"E50"),sQuery(id+"F36.wireOp",EDGE,"E51"),sQuery(id+"F36.wireOp",EDGE,"E52"),sQuery(id+"F36.wireOp",EDGE,"E53")])]});
            var Q17;
            Q17=makeQuery(id+"F39.opPattern","COPY",BODY,{"derivedFrom":makeQuery(id+"F37.opExtrude","SWEPT_BODY",BODY,{"disambiguationData":[OSD([sQuery(id+"F36.wireOp",EDGE,"E49"),sQuery(id+"F36.wireOp",EDGE,"E50"),sQuery(id+"F36.wireOp",EDGE,"E51"),sQuery(id+"F36.wireOp",EDGE,"E52"),sQuery(id+"F36.wireOp",EDGE,"E53")])]}),"instanceName":"1"});
            var Q18;
            Q18=makeQuery(id+"F43.opExtrude","SWEPT_BODY",BODY,{"disambiguationData":[OSD([sQuery(id+"F42.wireOp",EDGE,"E54"),sQuery(id+"F42.wireOp",EDGE,"E55"),sQuery(id+"F42.wireOp",EDGE,"E56"),sQuery(id+"F42.wireOp",EDGE,"E57"),sQuery(id+"F42.wireOp",EDGE,"E58")])]});
            var Q19;
            Q19=makeQuery(id+"F45.opPattern","COPY",BODY,{"derivedFrom":makeQuery(id+"F43.opExtrude","SWEPT_BODY",BODY,{"disambiguationData":[OSD([sQuery(id+"F42.wireOp",EDGE,"E54"),sQuery(id+"F42.wireOp",EDGE,"E55"),sQuery(id+"F42.wireOp",EDGE,"E56"),sQuery(id+"F42.wireOp",EDGE,"E57"),sQuery(id+"F42.wireOp",EDGE,"E58")])]}),"instanceName":"1"});
            deleteBodies(context, id + "F46", {"entities" : qUnion([Q0, Q1, Q2, Q3, Q4, Q5, Q6, Q7, Q8, Q9, Q10, Q11, Q12, Q13, Q14, Q15, Q16, Q17, Q18, Q19])});
        }
    });
